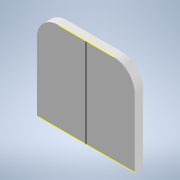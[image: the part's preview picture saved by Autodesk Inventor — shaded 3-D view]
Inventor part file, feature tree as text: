
AUTODESK INVENTOR PART (.ipt)
format: ipt  version: 2020 (Build 240168000, 168)  size: 104,960 bytes
history: native  units: mm
features: sketch x2, other x1, extrude x1, fillet x1, hole x1
ambient origin geometry x8: Origin, YZ Plane, XZ Plane, XY Plane, X Axis, Y Axis, Z Axis, Center Point
bodies: Body1 (feature_tree)
feature tree (6):
  other  "Твердое тело1"
  extrude  "Выдавливание1"  Depth=11.6mm
  fillet  "Сопряжение1"  Radius=10.6mm
  hole  "Отверстие1"  [1 undecoded]
  sketch  "Эскиз1"
  sketch  "Эскиз2"
note: 1 required parameter value undecoded (feature->parameter linkage not recoverable at this tier; creation-order binding heuristic only, values carry confidence <= 0.55)
